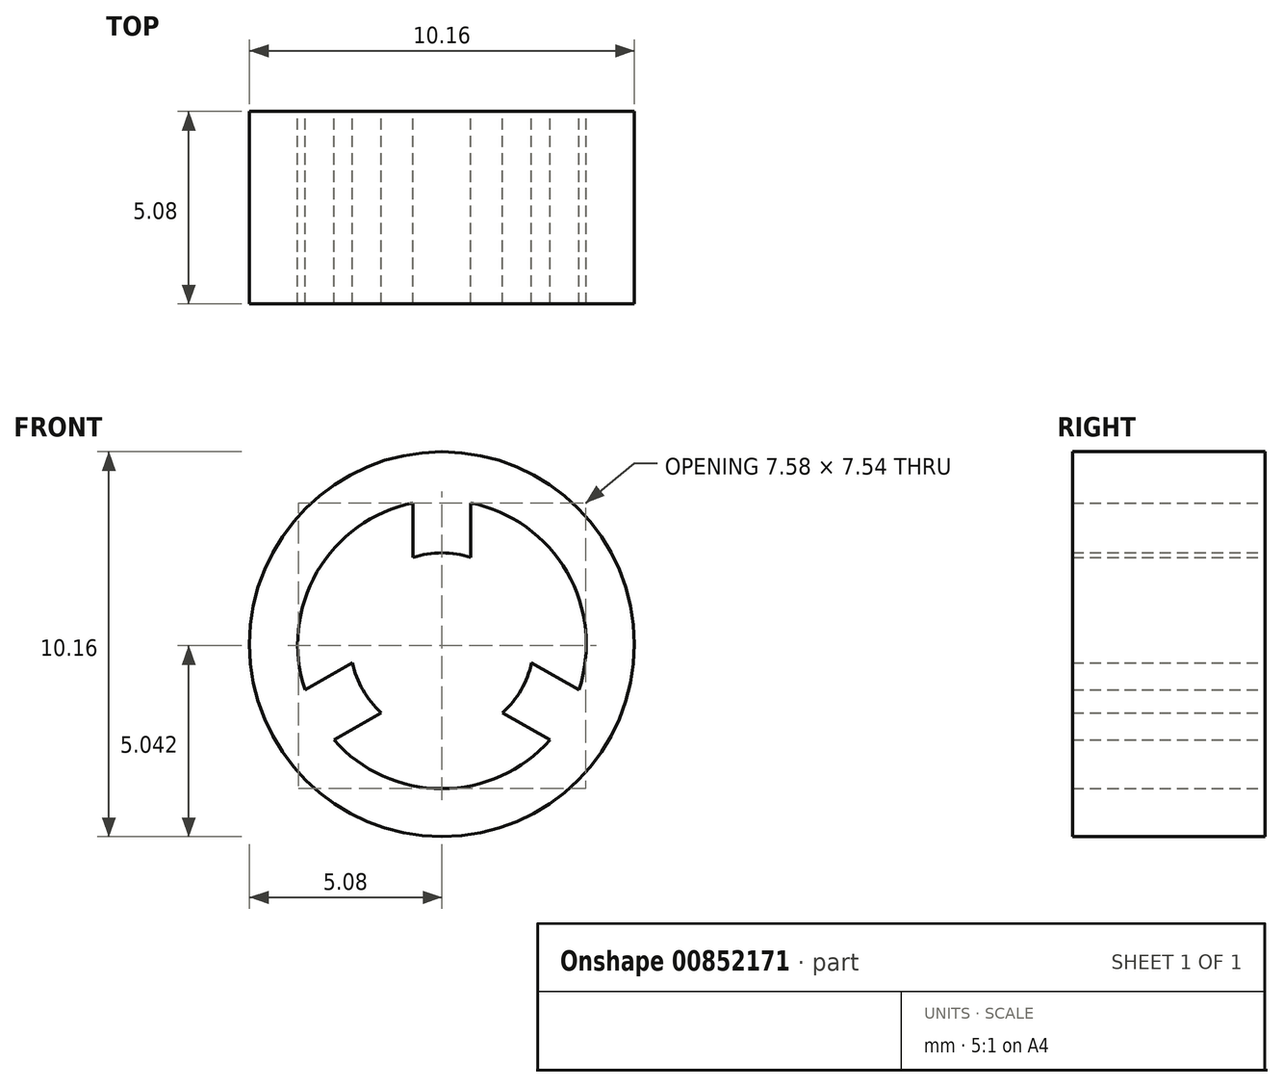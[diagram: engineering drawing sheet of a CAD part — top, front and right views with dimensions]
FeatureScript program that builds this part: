
annotation { "Feature Type Name" : "Feature", "Feature Type Description" : "" }
export const myFeature = defineFeature(function(context is Context, id is Id, definition is map)
    precondition{}
    {
        {
            var Q0;
            Q0=qCreatedBy(makeId("Front.planeOp"),FACE);
            var sketch = newSketch(context, id + "F0", { "sketchPlane" : qUnion([Q0])});
            skArc(sketch, "E0", {"start": v(0.76, 2.29) * mm, "mid": v(0, 2.41) * mm, "end": v(-0.76, 2.29) * mm});
            skCircle(sketch, "E1", {"center": v(0, 0) * mm, "radius": 5.08 * mm});
            skArc(sketch, "E2", {"start": v(3.61, -1.2) * mm, "mid": v(3.3, 1.9) * mm, "end": v(0.76, 3.73) * mm});
            skLineSegment(sketch, "E3", {"start": v(-0.76, 3.73) * mm, "end": v(-0.76, 2.29) * mm});
            skLineSegment(sketch, "E4", {"start": v(0.76, 3.73) * mm, "end": v(0.76, 2.29) * mm});
            skLineSegment(sketch, "E5.1.0", {"start": v(-3.61, -1.2) * mm, "end": v(-2.36, -0.48) * mm});
            skLineSegment(sketch, "E5.1.1", {"start": v(-2.85, -2.53) * mm, "end": v(-1.6, -1.8) * mm});
            skLineSegment(sketch, "E5.2.0", {"start": v(2.85, -2.53) * mm, "end": v(1.6, -1.8) * mm});
            skLineSegment(sketch, "E5.2.1", {"start": v(3.61, -1.2) * mm, "end": v(2.36, -0.48) * mm});
            skArc(sketch, "E6.trimOffspring", {"start": v(-2.36, -0.48) * mm, "mid": v(-2.09, -1.2) * mm, "end": v(-1.6, -1.8) * mm});
            skArc(sketch, "E7.trimOffspring", {"start": v(1.6, -1.8) * mm, "mid": v(2.09, -1.2) * mm, "end": v(2.36, -0.48) * mm});
            skArc(sketch, "E8.trimOffspring", {"start": v(-0.76, 3.73) * mm, "mid": v(-3.3, 1.9) * mm, "end": v(-3.61, -1.2) * mm});
            skArc(sketch, "E9.trimOffspring", {"start": v(-2.85, -2.53) * mm, "mid": v(0, -3.81) * mm, "end": v(2.85, -2.53) * mm});
            skSolve(sketch);
        }
        {
            var Q0;
            Q0 = qSketchRegion(id + "F0", true);
            extrude(context, id + "F1", {"entities" : qUnion([Q0]), "depth" : 5.08 * mm, "offsetDistance" : 25.4 * mm});
        }
    });
